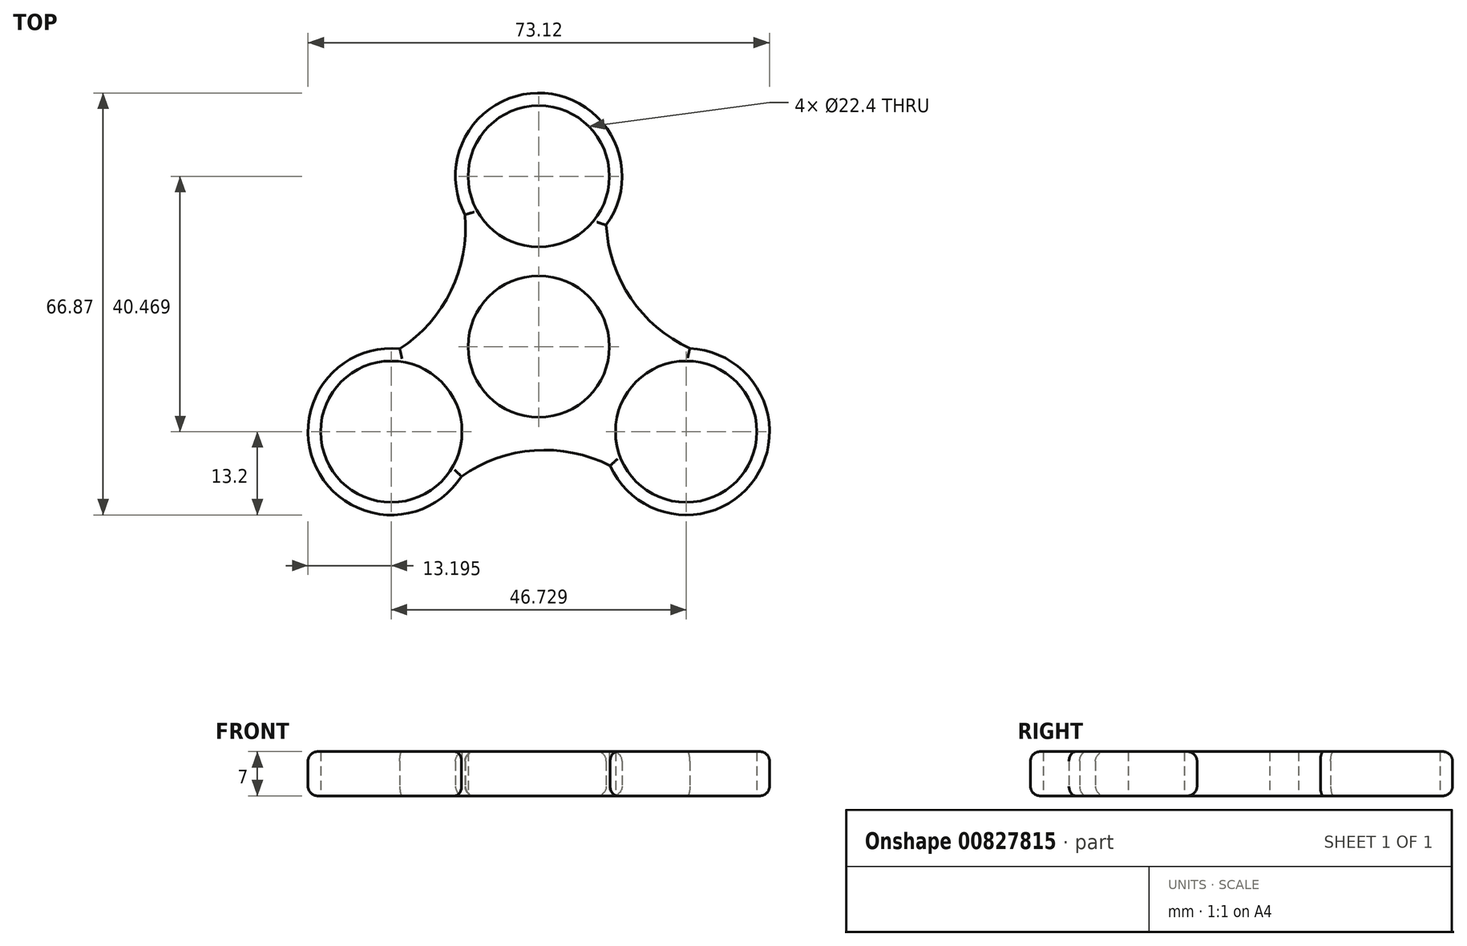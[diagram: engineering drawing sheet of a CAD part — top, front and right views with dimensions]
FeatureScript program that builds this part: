
annotation { "Feature Type Name" : "Feature", "Feature Type Description" : "" }
export const myFeature = defineFeature(function(context is Context, id is Id, definition is map)
    precondition{}
    {
        {
            var Q0;
            Q0=qCreatedBy(makeId("Top.planeOp"),FACE);
            var sketch = newSketch(context, id + "F0", { "sketchPlane" : qUnion([Q0])});
            skCircle(sketch, "E0", {"center": v(0, 0) * mm, "radius": 11.2 * mm});
            skCircle(sketch, "E1", {"center": v(0, 26.98) * mm, "radius": 11.2 * mm});
            skArc(sketch, "E2", {"start": v(10.7, 19.25) * mm, "mid": v(0.96, 40.14) * mm, "end": v(-11.7, 20.88) * mm});
            skArc(sketch, "E3.1.0", {"start": v(-22.02, -0.36) * mm, "mid": v(-35.25, -19.24) * mm, "end": v(-12.23, -20.58) * mm});
            skCircle(sketch, "E3.1.1", {"center": v(-23.36, -13.49) * mm, "radius": 11.2 * mm});
            skArc(sketch, "E3.2.0", {"start": v(11.32, -18.9) * mm, "mid": v(34.29, -20.9) * mm, "end": v(23.94, -0.3) * mm});
            skCircle(sketch, "E3.2.1", {"center": v(23.36, -13.49) * mm, "radius": 11.2 * mm});
            skArc(sketch, "E4", {"start": v(10.7, 19.25) * mm, "mid": v(14.6, 7.63) * mm, "end": v(23.94, -0.3) * mm});
            skArc(sketch, "E5.1.0", {"start": v(-22.02, -0.36) * mm, "mid": v(-13.9, 8.83) * mm, "end": v(-11.7, 20.88) * mm});
            skArc(sketch, "E5.2.0", {"start": v(11.32, -18.9) * mm, "mid": v(-0.7, -16.46) * mm, "end": v(-12.23, -20.58) * mm});
            skSolve(sketch);
        }
        {
            var Q0;
            Q0=makeQuery(id+"F0.imprint","IMPRINT",FACE,{"disambiguationData":[TD([[makeQuery(id+"F0.imprint","IMPRINT",EDGE,{"derivedFrom":sQuery(id+"F0.wireOp",EDGE,"E0")}),-1.0]])]});
            extrude(context, id + "F1", {"entities" : qUnion([Q0]), "depth" : 7 * mm, "offsetDistance" : 25 * mm});
        }
        {
            var Q0;
            Q0=makeQuery(id+"F1.opExtrude","CAP_EDGE",EDGE,{"disambiguationData":[OSD([sQuery(id+"F0.wireOp",EDGE,"E5.2.0")])],"isStart":false});
            var Q1;
            Q1=makeQuery(id+"F1.opExtrude","CAP_EDGE",EDGE,{"disambiguationData":[OSD([sQuery(id+"F0.wireOp",EDGE,"E3.1.0")])],"isStart":false});
            var Q2;
            Q2=makeQuery(id+"F1.opExtrude","CAP_EDGE",EDGE,{"disambiguationData":[OSD([sQuery(id+"F0.wireOp",EDGE,"E5.1.0")])],"isStart":false});
            var Q3;
            Q3=makeQuery(id+"F1.opExtrude","CAP_EDGE",EDGE,{"disambiguationData":[OSD([sQuery(id+"F0.wireOp",EDGE,"E2")])],"isStart":false});
            var Q4;
            Q4=makeQuery(id+"F1.opExtrude","CAP_EDGE",EDGE,{"disambiguationData":[OSD([sQuery(id+"F0.wireOp",EDGE,"E4")])],"isStart":false});
            var Q5;
            Q5=makeQuery(id+"F1.opExtrude","CAP_EDGE",EDGE,{"disambiguationData":[OSD([sQuery(id+"F0.wireOp",EDGE,"E3.2.0")])],"isStart":false});
            fillet(context, id + "F2", {"entities" : qUnion([Q0, Q1, Q2, Q3, Q4, Q5]), "radius" : 1.5 * mm, "tangentPropagation" : true, "allowEdgeOverflow" : false});
        }
        {
            var Q0;
            Q0=makeQuery(id+"F1.opExtrude","CAP_EDGE",EDGE,{"disambiguationData":[OSD([sQuery(id+"F0.wireOp",EDGE,"E3.1.0")])],"isStart":true});
            var Q1;
            Q1=makeQuery(id+"F1.opExtrude","CAP_EDGE",EDGE,{"disambiguationData":[OSD([sQuery(id+"F0.wireOp",EDGE,"E5.2.0")])],"isStart":true});
            var Q2;
            Q2=makeQuery(id+"F1.opExtrude","CAP_EDGE",EDGE,{"disambiguationData":[OSD([sQuery(id+"F0.wireOp",EDGE,"E3.2.0")])],"isStart":true});
            var Q3;
            Q3=makeQuery(id+"F1.opExtrude","CAP_EDGE",EDGE,{"disambiguationData":[OSD([sQuery(id+"F0.wireOp",EDGE,"E4")])],"isStart":true});
            var Q4;
            Q4=makeQuery(id+"F1.opExtrude","CAP_EDGE",EDGE,{"disambiguationData":[OSD([sQuery(id+"F0.wireOp",EDGE,"E2")])],"isStart":true});
            var Q5;
            Q5=makeQuery(id+"F1.opExtrude","CAP_EDGE",EDGE,{"disambiguationData":[OSD([sQuery(id+"F0.wireOp",EDGE,"E5.1.0")])],"isStart":true});
            fillet(context, id + "F3", {"entities" : qUnion([Q0, Q1, Q2, Q3, Q4, Q5]), "radius" : 1.5 * mm, "tangentPropagation" : true, "allowEdgeOverflow" : false});
        }
    });
